# Revit family: Door_RecessedPanel_Ambico_Double-1x1
name_source: partatom
category: Doors
units: mm (PartAtom-declared; Revit-internal decimal feet)

## family parameters
Always vertical = Yes
Classification Number = 23.30.10.14.11
Cut with Voids When Loaded = No
Host = Wall
Room Calculation Point = No
Shared = No

## types (1)
- as Specified
    ADA Compliant = Yes
    Construction Details = http://www.arcat.com
    Description = Ambico Recessed Panel Steel Door - Pair Configuration as Specified
    Expected Lifespan (Years) = 0
    Fire Rating = NFR
    Frame Finish = Metal - Bronze - Ambico - Architectural
    Frame Thickness = 0' - 5 7/8"
    Frame Width = 0' - 2"
    Function = Interior
    Green Building-LEED = http://www.arcat.com
    Handle Height = 3' - 0"
    Hardware Finish = Metal - Stainless Steel - Ambico - 4 Finish
    Heat Transfer Coefficient (U) = 0.1 BTU/(h·ft²·°F)
    Height = 7' - 0"
    Installation-Fabrication = http://www.ambico.com
    Keynote = 08300
    Maintenance Schedule (Months) = 0
    Manufacturer = Ambico Limited
    Manufacturer Fax = 800-465-8561
    Manufacturer Website = http://www.ambico.com
    Model = Recessed Panel 1x1
    Panel Height = 6' - 11 3/4"
    Panel Material = Metal - Bronze - Ambico - Architectural
    Panel Width = 3' - 0"
    Product Data = http://www.arcat.com
    R = 0.0000 (h·ft²·°F)/BTU
    RO Offset = 0' - 0"
    Rail Height_Bottom = 1' - 0"
    Rail Height_Top = 0' - 5"
    Rough Height = 7' - 0"
    Rough Width = 6' - 0"
    SHGC = 0
    Sales Information = http://www.ambico.com
    Send Message = http://www.arcat.com Limited&coid=40356&rep=119&fax=800-465-8561&mf=
    Solar Heat Gain Coefficient = 0
    Sound Transmission Class (STC) = 0
    Specification = http://www.arcat.com
    Stile Width_Hinge Side = 0' - 5"
    Stile Width_Latch Side = 0' - 5"
    Thermal Resistance (R) = 0.0000 (h·ft²·°F)/BTU
    Thickness = 0' - 1 3/4"
    U = 0.1 BTU/(h·ft²·°F)
    URL = http://www.ambico.com
    VLT = 0
    Visual Light Transmittance = 0
    Wall Closure = By host
    Warranty Duration (Years) = 0
    Width = 6' - 0"

## geometry (parser evidence)
native form markers: Blend x16, Sweep x11
no freeform markers — native parametric forms only
